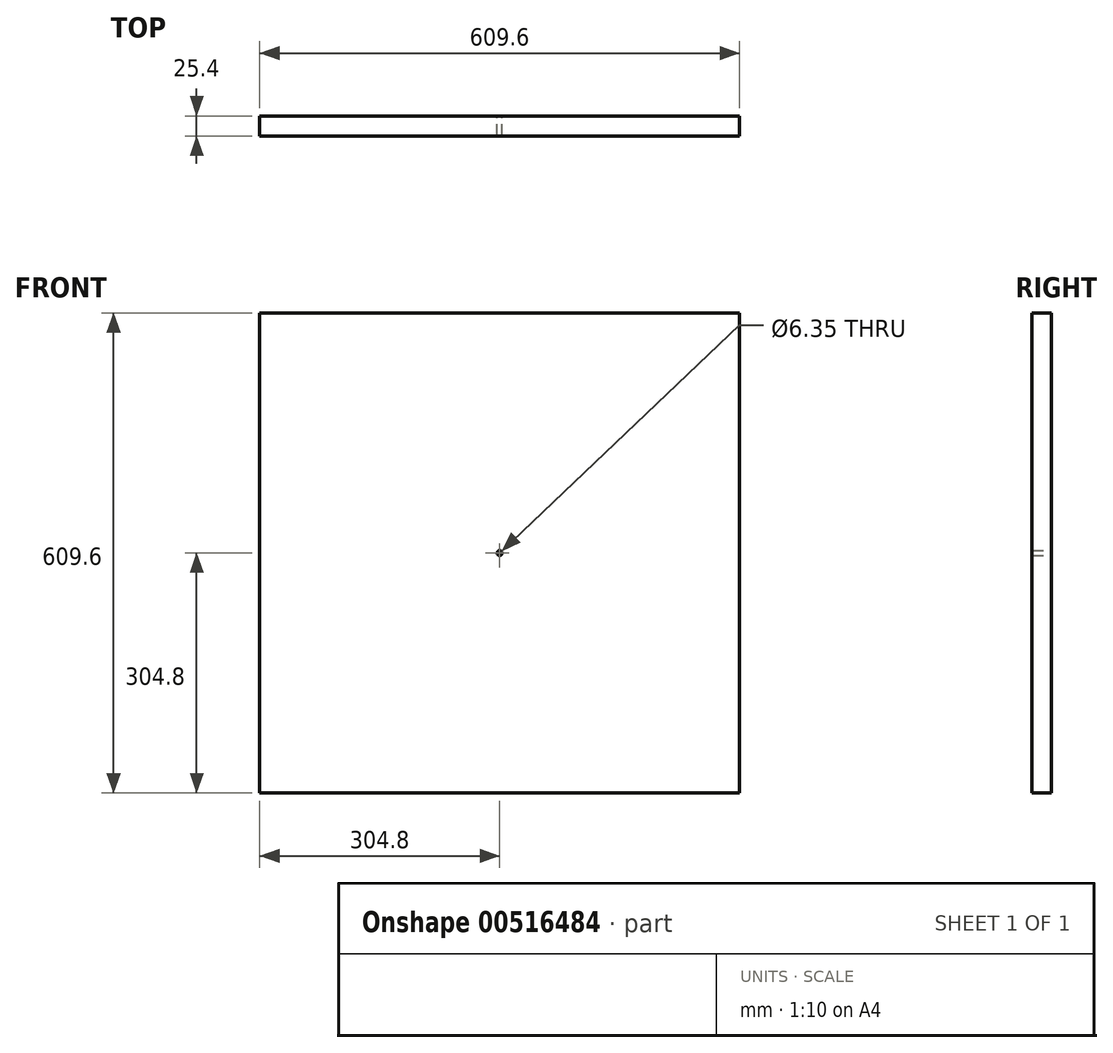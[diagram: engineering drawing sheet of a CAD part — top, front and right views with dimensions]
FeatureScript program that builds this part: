
annotation { "Feature Type Name" : "Feature", "Feature Type Description" : "" }
export const myFeature = defineFeature(function(context is Context, id is Id, definition is map)
    precondition{}
    {
        {
            var Q0;
            Q0=qCreatedBy(makeId("Front.planeOp"),FACE);
            var sketch = newSketch(context, id + "F0", { "sketchPlane" : qUnion([Q0])});
            skLineSegment(sketch, "E0.bottom", {"start": v(304.8, -304.8) * mm, "end": v(-304.8, -304.8) * mm});
            skLineSegment(sketch, "E0.top", {"start": v(304.8, 304.8) * mm, "end": v(-304.8, 304.8) * mm});
            skLineSegment(sketch, "E0.left", {"start": v(304.8, -304.8) * mm, "end": v(304.8, 304.8) * mm});
            skLineSegment(sketch, "E0.right", {"start": v(-304.8, -304.8) * mm, "end": v(-304.8, 304.8) * mm});
            skPoint(sketch, "E0.middle", {"position": v(0, 0) * mm});
            skCircle(sketch, "E1", {"center": v(0, 0) * mm, "radius": 3.18 * mm});
            skSolve(sketch);
        }
        {
            var Q0;
            Q0=makeQuery(id+"F0.imprint","IMPRINT",FACE,{"disambiguationData":[TD([[makeQuery(id+"F0.imprint","IMPRINT",EDGE,{"derivedFrom":sQuery(id+"F0.wireOp",EDGE,"E0.bottom")}),-1.0]])]});
            extrude(context, id + "F1", {"entities" : qUnion([Q0]), "depth" : 25.4 * mm, "offsetDistance" : 25.4 * mm});
        }
    });
